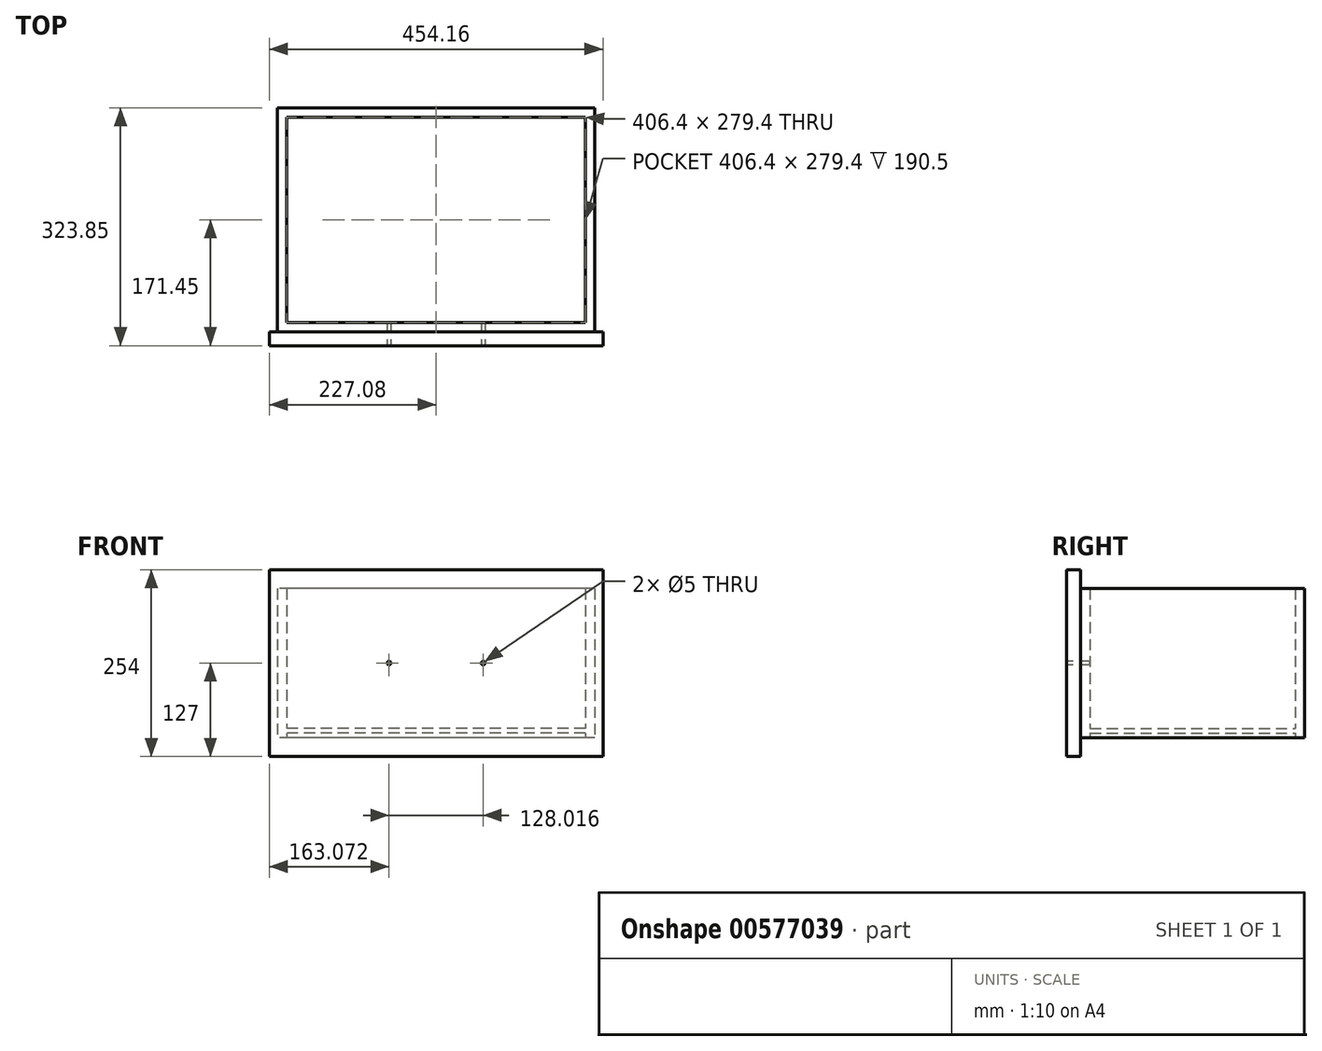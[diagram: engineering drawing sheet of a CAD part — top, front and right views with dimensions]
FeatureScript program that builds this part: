
annotation { "Feature Type Name" : "Feature", "Feature Type Description" : "" }
export const myFeature = defineFeature(function(context is Context, id is Id, definition is map)
    precondition{}
    {
        {
            var Q0;
            Q0=qCreatedBy(makeId("Top.planeOp"),FACE);
            var sketch = newSketch(context, id + "F0", { "sketchPlane" : qUnion([Q0])});
            skLineSegment(sketch, "E0.bottom", {"start": v(215.9, 152.4) * mm, "end": v(-215.9, 152.4) * mm});
            skLineSegment(sketch, "E0.top", {"start": v(215.9, -152.4) * mm, "end": v(-215.9, -152.4) * mm});
            skLineSegment(sketch, "E0.left", {"start": v(215.9, 152.4) * mm, "end": v(215.9, -152.4) * mm});
            skLineSegment(sketch, "E0.right", {"start": v(-215.9, 152.4) * mm, "end": v(-215.9, -152.4) * mm});
            skPoint(sketch, "E0.middle", {"position": v(0, 0) * mm});
            skLineSegment(sketch, "E1.bottom", {"start": v(203.2, 139.7) * mm, "end": v(-203.2, 139.7) * mm});
            skLineSegment(sketch, "E1.top", {"start": v(203.2, -139.7) * mm, "end": v(-203.2, -139.7) * mm});
            skLineSegment(sketch, "E1.left", {"start": v(203.2, 139.7) * mm, "end": v(203.2, -139.7) * mm});
            skLineSegment(sketch, "E1.right", {"start": v(-203.2, 139.7) * mm, "end": v(-203.2, -139.7) * mm});
            skSolve(sketch);
        }
        {
            var Q0;
            Q0=makeQuery(id+"F0.imprint","IMPRINT",FACE,{"disambiguationData":[TD([[makeQuery(id+"F0.imprint","IMPRINT",EDGE,{"derivedFrom":sQuery(id+"F0.wireOp",EDGE,"E0.bottom")}),1.0]])]});
            extrude(context, id + "F1", {"entities" : qUnion([Q0]), "depth" : 203.2 * mm, "offsetDistance" : 25.4 * mm});
        }
        {
            var Q0;
            Q0=makeQuery(id+"F1.opExtrude","SWEPT_FACE",FACE,{"disambiguationData":[OSD([sQuery(id+"F0.wireOp",EDGE,"E1.right")])]});
            var sketch = newSketch(context, id + "F2", { "sketchPlane" : qUnion([Q0])});
            skLineSegment(sketch, "E2", {"start": v(-139.7, 0) * mm, "end": v(-139.7, 6.35) * mm});
            skLineSegment(sketch, "E3", {"start": v(-139.7, 6.35) * mm, "end": v(139.7, 6.35) * mm});
            skLineSegment(sketch, "E4", {"start": v(-139.7, 6.35) * mm, "end": v(-139.7, 12.7) * mm});
            skLineSegment(sketch, "E5", {"start": v(-139.7, 12.7) * mm, "end": v(139.7, 12.7) * mm});
            skSolve(sketch);
        }
        {
            var Q0;
            {var subQ0=sQuery(id+"F2.wireOp",EDGE,"E3");Q0=makeQuery(id+"F2.imprint","IMPRINT",FACE,{"disambiguationData":[TD([[makeQuery(id+"F2.imprint","IMPRINT",EDGE,{"derivedFrom":subQ0}),1.0]])]});}
            extrude(context, id + "F3", {"entities" : qUnion([Q0]), "operationType" : NewBodyOperationType.ADD, "endBound" : BoundingType.UP_TO_NEXT, "depth" : 25.4 * mm, "offsetDistance" : 25.4 * mm});
        }
        {
            var Q0;
            Q0=makeQuery(id+"F1.opExtrude","SWEPT_FACE",FACE,{"disambiguationData":[OSD([sQuery(id+"F0.wireOp",EDGE,"E0.top")])]});
            var sketch = newSketch(context, id + "F4", { "sketchPlane" : qUnion([Q0])});
            skLineSegment(sketch, "E6", {"start": v(0, 203.2) * mm, "end": v(0, 0) * mm});
            skLineSegment(sketch, "E7.bottom", {"start": v(227.08, 228.6) * mm, "end": v(-227.08, 228.6) * mm});
            skLineSegment(sketch, "E7.top", {"start": v(227.08, -25.4) * mm, "end": v(-227.08, -25.4) * mm});
            skLineSegment(sketch, "E7.left", {"start": v(227.08, 228.6) * mm, "end": v(227.08, -25.4) * mm});
            skLineSegment(sketch, "E7.right", {"start": v(-227.08, 228.6) * mm, "end": v(-227.08, -25.4) * mm});
            skPoint(sketch, "E7.middle", {"position": v(0, 101.6) * mm});
            skSolve(sketch);
        }
        {
            var Q0;
            Q0 = qSketchRegion(id + "F4", true);
            extrude(context, id + "F5", {"entities" : qUnion([Q0]), "operationType" : NewBodyOperationType.ADD, "depth" : 19.05 * mm, "offsetDistance" : 25.4 * mm});
        }
        {
            var Q0;
            Q0=makeQuery(id+"F5.opExtrude","CAP_FACE",FACE,{"disambiguationData":[OSD([sQuery(id+"F4.wireOp",EDGE,"E7.bottom"),sQuery(id+"F4.wireOp",EDGE,"E7.top"),sQuery(id+"F4.wireOp",EDGE,"E7.left"),sQuery(id+"F4.wireOp",EDGE,"E7.right")])],"isStart":false});
            var sketch = newSketch(context, id + "F6", { "sketchPlane" : qUnion([Q0])});
            skLineSegment(sketch, "E8", {"start": v(0, 228.6) * mm, "end": v(0, 101.6) * mm});
            skLineSegment(sketch, "E9", {"start": v(0, 101.6) * mm, "end": v(64, 101.6) * mm});
            skLineSegment(sketch, "E10", {"start": v(0, 101.6) * mm, "end": v(-64, 101.6) * mm});
            skPoint(sketch, "E11", {"position": v(-64, 101.6) * mm});
            skPoint(sketch, "E12", {"position": v(64, 101.6) * mm});
            skSolve(sketch);
        }
        {
            var Q0;
            Q0=sQuery(id+"F6.wireOp",VERTEX,"E11");
            var Q1;
            Q1=sQuery(id+"F6.wireOp",VERTEX,"E12");
            var Q2;
            Q2=makeQuery(id+"F1.opExtrude","SWEPT_BODY",BODY,{"disambiguationData":[OSD([sQuery(id+"F0.wireOp",EDGE,"E0.bottom"),sQuery(id+"F0.wireOp",EDGE,"E0.top"),sQuery(id+"F0.wireOp",EDGE,"E0.left"),sQuery(id+"F0.wireOp",EDGE,"E0.right"),sQuery(id+"F0.wireOp",EDGE,"E1.bottom"),sQuery(id+"F0.wireOp",EDGE,"E1.top"),sQuery(id+"F0.wireOp",EDGE,"E1.left"),sQuery(id+"F0.wireOp",EDGE,"E1.right")])]});
            hole(context, id + "F7", {"style" : HoleStyle.SIMPLE, "endStyle" : HoleEndStyle.BLIND, "holeDiameter" : 5 * mm, "majorDiameter" : 6.35 * mm, "holeDepth" : 31.75 * mm, "isTappedThrough" : true, "tappedDepth" : 12.7 * mm, "tapClearance" : 3, "startFromSketch" : true, "locations" : qUnion([Q0, Q1]), "scope" : qUnion([Q2])});
        }
    });
